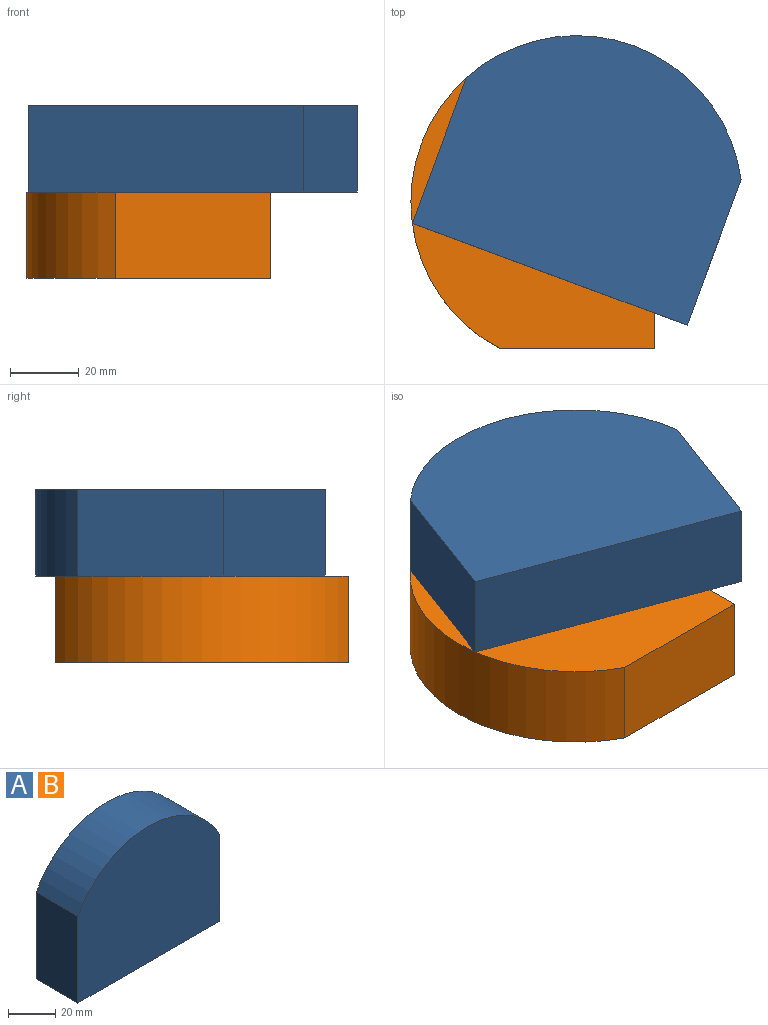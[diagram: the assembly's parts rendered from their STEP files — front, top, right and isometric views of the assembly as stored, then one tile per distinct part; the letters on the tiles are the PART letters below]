
ASSEMBLY  parts=2 mates=1
PART A: 6 faces, bbox 85x25x70.6 mm
  f0: plane 85x25mm, normal (0,0,-1), area 2125mm2, adj f1,f3,f4,f5
  f1: plane 45x25mm, normal (1,0,0), area 1125mm2, adj f0,f2,f4,f5
  f2: cylinder r=48.09mm len=85mm, axis (0,1,0), area 2606.1mm2, adj f1,f3,f4,f5
  f3: plane 45x25mm, normal (-1,0,0), area 1125mm2, adj f0,f2,f4,f5
  f4: plane 85x70.59mm, normal (0,-1,0), area 5375.3mm2, adj f0,f1,f2,f3
  f5: plane 85x70.59mm, normal (0,1,0), area 5375.3mm2, adj f0,f1,f2,f3
PART B: same geometry as A
PLACE A rot(axis=(-0.97,0.17,-0.17),91.8deg) t=(0,0,0)mm
PLACE B rot(axis=(0.58,-0.58,-0.58),120deg) t=(0,0,0)mm
MATE revolute A.f2 <-> B.f2  axis (0,0,-1) through (0,0,0)mm
